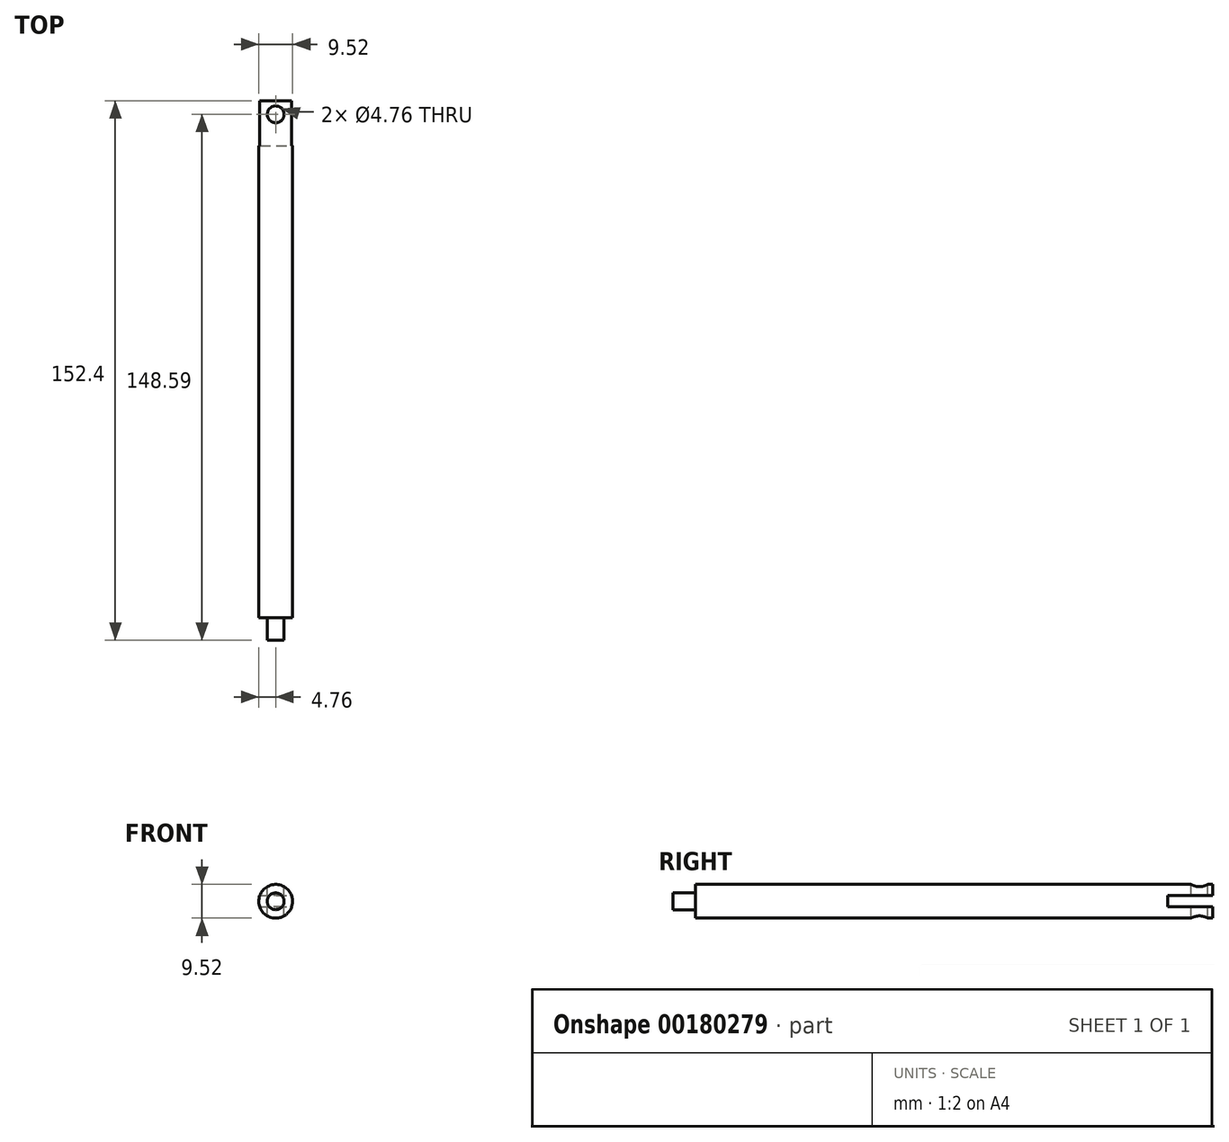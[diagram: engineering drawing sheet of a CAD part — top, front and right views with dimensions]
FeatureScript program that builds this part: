
annotation { "Feature Type Name" : "Feature", "Feature Type Description" : "" }
export const myFeature = defineFeature(function(context is Context, id is Id, definition is map)
    precondition{}
    {
        {
            var Q0;
            Q0=qCreatedBy(makeId("Front.planeOp"),FACE);
            var sketch = newSketch(context, id + "F0", { "sketchPlane" : qUnion([Q0])});
            skCircle(sketch, "E0", {"center": v(0, 0) * mm, "radius": 4.76 * mm});
            skSolve(sketch);
        }
        {
            var Q0;
            Q0=qSketchRegion(id+"F0",true);
            extrude(context, id + "F1", {"entities" : qUnion([Q0]), "depth" : 152.4 * mm});
        }
        {
            var Q0;
            Q0=qCreatedBy(makeId("Right.planeOp"),FACE);
            var sketch = newSketch(context, id + "F2", { "sketchPlane" : qUnion([Q0])});
            skLineSegment(sketch, "E1.bottom", {"start": v(-146.05, 7.12) * mm, "end": v(-152.4, 7.12) * mm});
            skLineSegment(sketch, "E1.top", {"start": v(-146.05, 2.38) * mm, "end": v(-152.4, 2.38) * mm});
            skLineSegment(sketch, "E1.left", {"start": v(-146.05, 7.12) * mm, "end": v(-146.05, 2.38) * mm});
            skLineSegment(sketch, "E1.right", {"start": v(-152.4, 7.12) * mm, "end": v(-152.4, 2.38) * mm});
            skLineSegment(sketch, "E2", {"start": v(0, 0) * mm, "end": v(-50.7, 0) * mm, "construction": true});
            skSolve(sketch);
        }
        {
            var Q0;
            Q0=makeQuery(id+"F2.imprint","IMPRINT",FACE,{"disambiguationData":[TD([[makeQuery(id+"F2.imprint","IMPRINT",EDGE,{"derivedFrom":sQuery(id+"F2.wireOp",EDGE,"E1.bottom")}),1.0]])]});
            var Q1;
            Q1=sQuery(id+"F2.wireOp",EDGE,"E1.top");
            var Q2;
            Q2=sQuery(id+"F2.wireOp",EDGE,"E1.left");
            var Q3;
            Q3=sQuery(id+"F2.wireOp",EDGE,"E1.right");
            var Q4;
            Q4=sQuery(id+"F2.wireOp",EDGE,"E1.bottom");
            var Q5;
            Q5=sQuery(id+"F2.wireOp",EDGE,"E2");
            revolve(context, id + "F3", {"operationType" : NewBodyOperationType.REMOVE, "entities" : qUnion([Q0]), "surfaceEntities" : qUnion([Q1, Q2, Q3, Q4]), "axis" : qUnion([Q5]), "revolveType" : RevolveType.FULL});
        }
        {
            var Q0;
            Q0=qCreatedBy(makeId("Right.planeOp"),FACE);
            var sketch = newSketch(context, id + "F4", { "sketchPlane" : qUnion([Q0])});
            skLineSegment(sketch, "E3", {"start": v(0, 0) * mm, "end": v(0, 1.59) * mm});
            skLineSegment(sketch, "E4", {"start": v(0, 1.59) * mm, "end": v(-12.7, 1.59) * mm});
            skLineSegment(sketch, "E5", {"start": v(-12.7, 1.59) * mm, "end": v(-12.7, 0) * mm});
            skLineSegment(sketch, "E6.MirrorCS", {"start": v(-12.7, -1.59) * mm, "end": v(-12.7, 0) * mm});
            skLineSegment(sketch, "E7.MirrorCS", {"start": v(0, 0) * mm, "end": v(0, -1.59) * mm});
            skLineSegment(sketch, "E8.MirrorCS", {"start": v(0, -1.59) * mm, "end": v(-12.7, -1.59) * mm});
            skLineSegment(sketch, "E9.bottom", {"start": v(0, 3.18) * mm, "end": v(-12.7, 3.17) * mm});
            skLineSegment(sketch, "E9.top", {"start": v(0, 5.53) * mm, "end": v(-12.7, 5.53) * mm});
            skLineSegment(sketch, "E9.left", {"start": v(0, 3.18) * mm, "end": v(0, 5.53) * mm});
            skLineSegment(sketch, "E9.right", {"start": v(-12.7, 3.17) * mm, "end": v(-12.7, 5.53) * mm});
            skLineSegment(sketch, "E10.MirrorCS", {"start": v(-12.7, -3.17) * mm, "end": v(-12.7, -5.53) * mm});
            skLineSegment(sketch, "E11.MirrorCS", {"start": v(0, -3.18) * mm, "end": v(0, -5.53) * mm});
            skLineSegment(sketch, "E12.MirrorCS", {"start": v(0, -3.18) * mm, "end": v(-12.7, -3.17) * mm});
            skLineSegment(sketch, "E13.MirrorCS", {"start": v(0, -5.53) * mm, "end": v(-12.7, -5.53) * mm});
            skSolve(sketch);
        }
        {
            var Q0;
            Q0=makeQuery(id+"F4.imprint","IMPRINT",FACE,{"disambiguationData":[TD([[makeQuery(id+"F4.imprint","IMPRINT",EDGE,{"derivedFrom":sQuery(id+"F4.wireOp",EDGE,"E3")}),1.0]])]});
            extrude(context, id + "F5", {"entities" : qUnion([Q0]), "operationType" : NewBodyOperationType.REMOVE, "endBound" : BoundingType.THROUGH_ALL, "oppositeDirection" : true, "depth" : 25.4 * mm, "hasSecondDirection" : true, "secondDirectionBound" : SecondDirectionBoundingType.THROUGH_ALL, "secondDirectionOppositeDirection" : false, "secondDirectionDepth" : 25.4 * mm});
        }
        {
            var Q0;
            Q0=qCreatedBy(makeId("Top.planeOp"),FACE);
            var sketch = newSketch(context, id + "F6", { "sketchPlane" : qUnion([Q0])});
            skCircle(sketch, "E14", {"center": v(0, -3.81) * mm, "radius": 2.38 * mm});
            skSolve(sketch);
        }
        {
            var Q0;
            Q0=qSketchRegion(id+"F6",true);
            extrude(context, id + "F7", {"entities" : qUnion([Q0]), "operationType" : NewBodyOperationType.REMOVE, "endBound" : BoundingType.SYMMETRIC, "oppositeDirection" : true, "depth" : 25.4 * mm, "hasSecondDirection" : true, "secondDirectionBound" : SecondDirectionBoundingType.UP_TO_SURFACE, "secondDirectionOppositeDirection" : false, "secondDirectionDepth" : 25.4 * mm});
        }
    });
